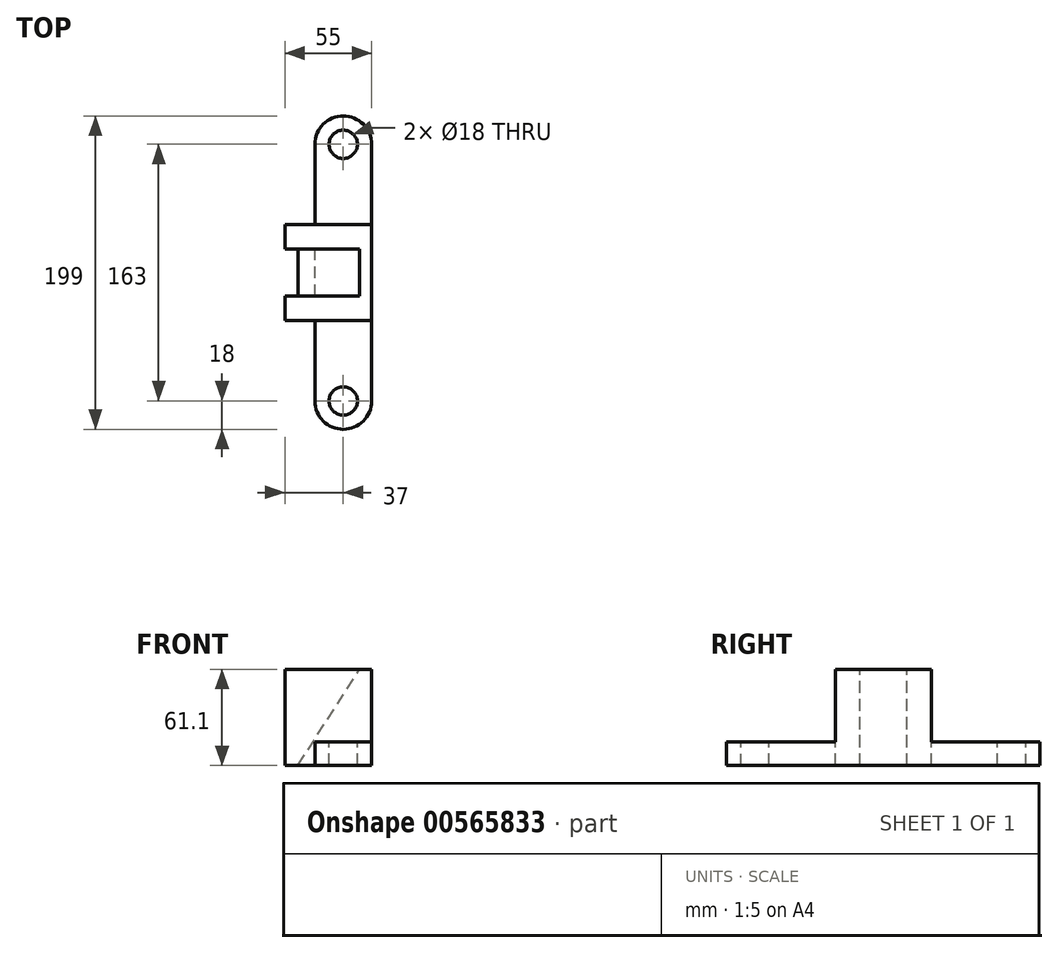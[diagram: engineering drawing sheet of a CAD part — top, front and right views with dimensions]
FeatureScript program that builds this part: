
annotation { "Feature Type Name" : "Feature", "Feature Type Description" : "" }
export const myFeature = defineFeature(function(context is Context, id is Id, definition is map)
    precondition{}
    {
        {
            var Q0;
            Q0=qCreatedBy(makeId("Right.planeOp"),FACE);
            var sketch = newSketch(context, id + "F0", { "sketchPlane" : qUnion([Q0])});
            skLineSegment(sketch, "E0.bottom", {"start": v(-30.5, 30.5) * mm, "end": v(30.5, 30.5) * mm});
            skLineSegment(sketch, "E0.top", {"start": v(-30.5, -30.5) * mm, "end": v(30.5, -30.5) * mm});
            skLineSegment(sketch, "E0.left", {"start": v(-30.5, 30.5) * mm, "end": v(-30.5, -30.5) * mm});
            skLineSegment(sketch, "E0.right", {"start": v(30.5, 30.5) * mm, "end": v(30.5, -30.5) * mm});
            skLineSegment(sketch, "E1", {"start": v(-30.5, -15.5) * mm, "end": v(-81.5, -15.5) * mm});
            skLineSegment(sketch, "E2", {"start": v(-81.5, -15.5) * mm, "end": v(-81.5, -30.5) * mm});
            skLineSegment(sketch, "E3", {"start": v(-81.5, -30.5) * mm, "end": v(-30.5, -30.5) * mm});
            skLineSegment(sketch, "E4", {"start": v(30.5, -15.5) * mm, "end": v(81.5, -15.5) * mm});
            skLineSegment(sketch, "E5", {"start": v(81.5, -15.5) * mm, "end": v(81.5, -30.5) * mm});
            skLineSegment(sketch, "E6", {"start": v(81.5, -30.5) * mm, "end": v(30.5, -30.5) * mm});
            skLineSegment(sketch, "E7", {"start": v(-81.5, -15.5) * mm, "end": v(-99.5, -15.5) * mm});
            skLineSegment(sketch, "E8", {"start": v(-99.5, -15.5) * mm, "end": v(-99.5, -30.6) * mm});
            skLineSegment(sketch, "E9", {"start": v(-99.5, -30.6) * mm, "end": v(-81.5, -30.5) * mm});
            skLineSegment(sketch, "E10", {"start": v(81.5, -15.5) * mm, "end": v(99.5, -15.5) * mm});
            skLineSegment(sketch, "E11", {"start": v(99.5, -15.5) * mm, "end": v(99.5, -30.6) * mm});
            skLineSegment(sketch, "E12", {"start": v(99.5, -30.6) * mm, "end": v(81.5, -30.5) * mm});
            skSolve(sketch);
        }
        {
            var Q0;
            Q0=qSketchRegion(id+"F0",true);
            extrude(context, id + "F1", {"entities" : qUnion([Q0]), "depth" : 36 * mm});
        }
        {
            var Q0;
            Q0=makeQuery(id+"F1.opExtrude","SWEPT_FACE",FACE,{"disambiguationData":[OSD([sQuery(id+"F0.wireOp",EDGE,"E0.bottom")])]});
            var sketch = newSketch(context, id + "F2", { "sketchPlane" : qUnion([Q0])});
            skLineSegment(sketch, "E13", {"start": v(36, -30.5) * mm, "end": v(36, 30.5) * mm});
            skLineSegment(sketch, "E14", {"start": v(36, 30.5) * mm, "end": v(-19, 30.5) * mm});
            skLineSegment(sketch, "E15", {"start": v(-19, 30.5) * mm, "end": v(-19, 15) * mm});
            skLineSegment(sketch, "E16", {"start": v(-19, 15) * mm, "end": v(28, 15) * mm});
            skLineSegment(sketch, "E17", {"start": v(28, 15) * mm, "end": v(28, -15) * mm});
            skLineSegment(sketch, "E18", {"start": v(28, -15) * mm, "end": v(-19, -15) * mm});
            skLineSegment(sketch, "E19", {"start": v(-19, -15) * mm, "end": v(-19, -30.5) * mm});
            skLineSegment(sketch, "E20", {"start": v(-19, -30.5) * mm, "end": v(0, -30.5) * mm});
            skPoint(sketch, "E21.center.orphan", {"position": v(18, 81.5) * mm});
            skPoint(sketch, "E22.center.orphan", {"position": v(18, -81.5) * mm});
            skLineSegment(sketch, "E23", {"start": v(-19, 15) * mm, "end": v(-19, -15) * mm});
            skCircle(sketch, "E24", {"center": v(18, 81.5) * mm, "radius": 18 * mm});
            skCircle(sketch, "E25", {"center": v(18, -81.5) * mm, "radius": 18 * mm});
            skLineSegment(sketch, "E26", {"start": v(36, 99.5) * mm, "end": v(36, -99.5) * mm});
            skLineSegment(sketch, "E27", {"start": v(36, -99.5) * mm, "end": v(0, -99.5) * mm});
            skLineSegment(sketch, "E28", {"start": v(0, -99.5) * mm, "end": v(0, 99.5) * mm});
            skLineSegment(sketch, "E29", {"start": v(0, 99.5) * mm, "end": v(36, 99.5) * mm});
            skCircle(sketch, "E30", {"center": v(18, 81.5) * mm, "radius": 9 * mm});
            skCircle(sketch, "E31", {"center": v(18, -81.5) * mm, "radius": 9 * mm});
            skLineSegment(sketch, "E32", {"start": v(36, -30.5) * mm, "end": v(0, -30.5) * mm});
            skSolve(sketch);
        }
        {
            var Q0;
            Q0=qCreatedBy(makeId("Top.planeOp"),FACE);
            var sketch = newSketch(context, id + "F3", { "sketchPlane" : qUnion([Q0])});
            skCircle(sketch, "E33", {"center": v(18, 81.5) * mm, "radius": 9 * mm});
            skCircle(sketch, "E34", {"center": v(18, -81.5) * mm, "radius": 9 * mm});
            skSolve(sketch);
        }
        {
            var Q0;
            Q0=qSketchRegion(id+"F3",true);
            extrude(context, id + "F4", {"entities" : qUnion([Q0]), "operationType" : NewBodyOperationType.REMOVE, "oppositeDirection" : true, "depth" : 103.1 * mm});
        }
        {
            var Q0;
            Q0=qCreatedBy(makeId("Front.planeOp"),FACE);
            var sketch = newSketch(context, id + "F5", { "sketchPlane" : qUnion([Q0])});
            skLineSegment(sketch, "E35", {"start": v(36.36, 30.74) * mm, "end": v(-18.64, 30.74) * mm});
            skLineSegment(sketch, "E36", {"start": v(-18.64, 30.74) * mm, "end": v(-18.64, -30.26) * mm});
            skLineSegment(sketch, "E37", {"start": v(-18.64, -30.26) * mm, "end": v(36.36, -30.26) * mm});
            skLineSegment(sketch, "E38", {"start": v(36.36, -30.26) * mm, "end": v(36.36, 30.74) * mm});
            skLineSegment(sketch, "E39", {"start": v(-10.64, -30.26) * mm, "end": v(28.61, 30.74) * mm});
            skLineSegment(sketch, "E40", {"start": v(0, -30.26) * mm, "end": v(0, -13.73) * mm});
            skSolve(sketch);
        }
        {
            var Q0;
            {var subQ0=sQuery(id+"F5.wireOp",EDGE,"E36");Q0=makeQuery(id+"F5.imprint","IMPRINT",FACE,{"disambiguationData":[TD([[makeQuery(id+"F5.imprint","IMPRINT",EDGE,{"derivedFrom":subQ0}),1.0]])]});}
            extrude(context, id + "F6", {"entities" : qUnion([Q0]), "operationType" : NewBodyOperationType.REMOVE, "depth" : 15 * mm});
        }
        {
            var Q0;
            {var subQ0=sQuery(id+"F5.wireOp",EDGE,"E36");Q0=makeQuery(id+"F5.imprint","IMPRINT",FACE,{"disambiguationData":[TD([[makeQuery(id+"F5.imprint","IMPRINT",EDGE,{"derivedFrom":subQ0}),1.0]])]});}
            extrude(context, id + "F7", {"entities" : qUnion([Q0]), "operationType" : NewBodyOperationType.REMOVE, "oppositeDirection" : true, "depth" : 15 * mm});
        }
        {
            var Q0;
            {var subQ3=sQuery(id+"F2.wireOp",EDGE,"E15");Q0=makeQuery(id+"F2.imprint","IMPRINT",FACE,{"disambiguationData":[TD([[makeQuery(id+"F2.imprint","IMPRINT",EDGE,{"derivedFrom":subQ3}),1.0]])]});}
            var Q1;
            {var subQ0=sQuery(id+"F2.wireOp",EDGE,"E19");Q1=makeQuery(id+"F2.imprint","IMPRINT",FACE,{"disambiguationData":[TD([[makeQuery(id+"F2.imprint","IMPRINT",EDGE,{"derivedFrom":subQ0}),1.0]])]});}
            extrude(context, id + "F8", {"entities" : qUnion([Q0, Q1]), "operationType" : NewBodyOperationType.ADD, "oppositeDirection" : true, "depth" : 61 * mm});
        }
        {
            var Q0;
            {var subQ0=sQuery(id+"F2.wireOp",EDGE,"E29");var subQ1=sQuery(id+"F2.wireOp",EDGE,"E24");var subQ2=makeQuery(id+"F2.imprint","INTERSECT",VERTEX,{"disambiguationData":[OD(0.0)],"derivedFrom":[subQ1,subQ0]});Q0=makeQuery(id+"F2.imprint","IMPRINT",FACE,{"disambiguationData":[TD([[makeQuery(id+"F2.imprint","IMPRINT",EDGE,{"disambiguationData":[TD([[subQ2,1.0]])],"derivedFrom":subQ1}),-1.0]])]});}
            var Q1;
            {var subQ0=sQuery(id+"F2.wireOp",EDGE,"E29");var subQ1=sQuery(id+"F2.wireOp",EDGE,"E24");var subQ2=makeQuery(id+"F2.imprint","INTERSECT",VERTEX,{"disambiguationData":[OD(1.0)],"derivedFrom":[subQ1,subQ0]});Q1=makeQuery(id+"F2.imprint","IMPRINT",FACE,{"disambiguationData":[TD([[makeQuery(id+"F2.imprint","IMPRINT",EDGE,{"disambiguationData":[TD([[subQ2,-1.0]])],"derivedFrom":subQ1}),-1.0]])]});}
            extrude(context, id + "F9", {"entities" : qUnion([Q0, Q1]), "operationType" : NewBodyOperationType.REMOVE, "oppositeDirection" : true, "depth" : 100 * mm});
        }
        {
            var Q0;
            {var subQ0=sQuery(id+"F2.wireOp",EDGE,"E28");var subQ1=sQuery(id+"F2.wireOp",EDGE,"E25");var subQ2=makeQuery(id+"F2.imprint","INTERSECT",VERTEX,{"derivedFrom":[subQ1,subQ0]});Q0=makeQuery(id+"F2.imprint","IMPRINT",FACE,{"disambiguationData":[TD([[makeQuery(id+"F2.imprint","IMPRINT",EDGE,{"disambiguationData":[TD([[subQ2,-1.0]])],"derivedFrom":subQ1}),-1.0]])]});}
            var Q1;
            {var subQ0=sQuery(id+"F2.wireOp",EDGE,"E26");var subQ1=sQuery(id+"F2.wireOp",EDGE,"E25");var subQ2=makeQuery(id+"F2.imprint","INTERSECT",VERTEX,{"derivedFrom":[subQ1,subQ0]});Q1=makeQuery(id+"F2.imprint","IMPRINT",FACE,{"disambiguationData":[TD([[makeQuery(id+"F2.imprint","IMPRINT",EDGE,{"disambiguationData":[TD([[subQ2,1.0]])],"derivedFrom":subQ1}),-1.0]])]});}
            extrude(context, id + "F10", {"entities" : qUnion([Q0, Q1]), "operationType" : NewBodyOperationType.REMOVE, "oppositeDirection" : true, "depth" : 100 * mm});
        }
        {
            var Q0;
            {var subQ3=sQuery(id+"F5.wireOp",EDGE,"E40");Q0=makeQuery(id+"F5.imprint","IMPRINT",FACE,{"disambiguationData":[TD([[makeQuery(id+"F5.imprint","IMPRINT",EDGE,{"derivedFrom":subQ3}),1.0]])]});}
            extrude(context, id + "F11", {"entities" : qUnion([Q0]), "operationType" : NewBodyOperationType.ADD, "depth" : 25 * mm});
        }
        {
            var Q0;
            {var subQ3=sQuery(id+"F5.wireOp",EDGE,"E40");Q0=makeQuery(id+"F5.imprint","IMPRINT",FACE,{"disambiguationData":[TD([[makeQuery(id+"F5.imprint","IMPRINT",EDGE,{"derivedFrom":subQ3}),1.0]])]});}
            extrude(context, id + "F12", {"entities" : qUnion([Q0]), "operationType" : NewBodyOperationType.ADD, "oppositeDirection" : true, "depth" : 25 * mm});
        }
    });
